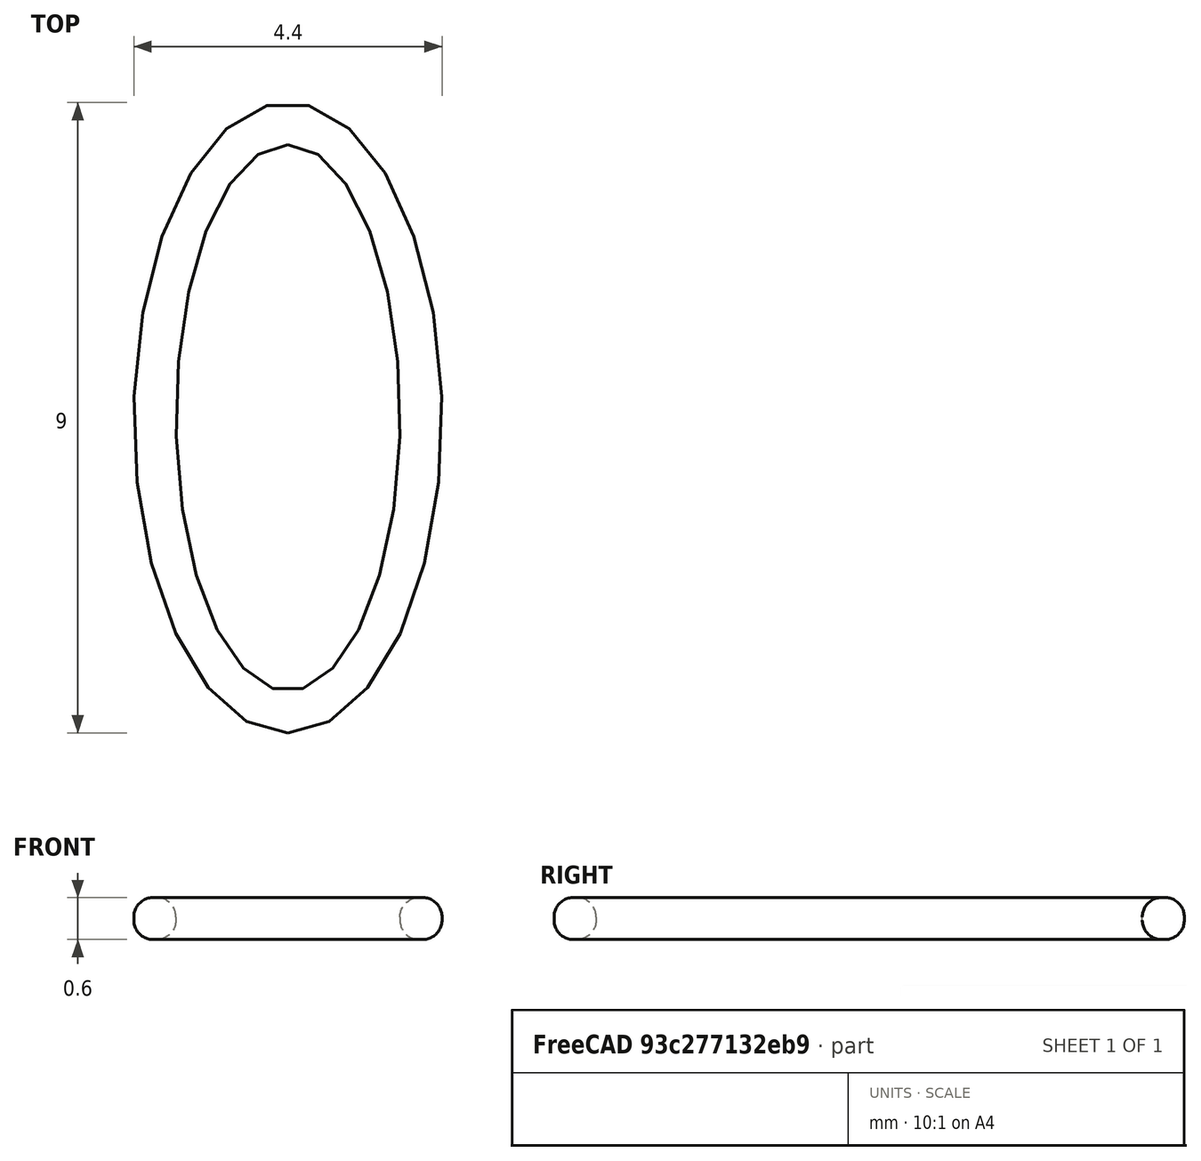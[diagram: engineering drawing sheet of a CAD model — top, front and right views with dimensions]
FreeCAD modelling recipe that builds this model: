
FCSTD DOCUMENT  (FreeCAD 0.16R6712 (Git))
Label: 0s
License: All rights reserved
LicenseURL: http://en.wikipedia.org/wiki/All_rights_reserved
objects: Sketcher::SketchObject×1, PartDesign::Pad×1, PartDesign::Fillet×1, Mesh::Feature×1
note: 4 computed .brp shape members not serialized (recipe doc carries the construction recipe); baked Part::Feature solids carry a one-line shape summary decoded from their .brp

FEATURE [Sketcher::SketchObject] Sketch
  sketch-geometry (10):
    g0: Ellipse CenterX=0 CenterY=4.5 CenterZ=0 NormalX=0 NormalY=0 NormalZ=1 MajorRadius=4.5 MinorRadius=2.2 AngleXU=-1.5708
    g1: LineSegment [constr] StartX=0 StartY=0 StartZ=0 EndX=0 EndY=9 EndZ=0
    g2: LineSegment [constr] StartX=2.2 StartY=4.5 StartZ=0 EndX=-2.2 EndY=4.5 EndZ=0
    g3: GeomPoint [constr] X=0 Y=0.574443 Z=0
    g4: GeomPoint [constr] X=0 Y=8.42556 Z=0
    g5: Ellipse CenterX=0 CenterY=4.5 CenterZ=0 NormalX=0 NormalY=0 NormalZ=1 MajorRadius=3.9 MinorRadius=1.6 AngleXU=1.5708
    g6: LineSegment [constr] StartX=0 StartY=8.4 StartZ=0 EndX=0 EndY=0.6 EndZ=0
    g7: LineSegment [constr] StartX=-1.6 StartY=4.5 StartZ=0 EndX=1.6 EndY=4.5 EndZ=0
    g8: GeomPoint [constr] X=0 Y=8.05668 Z=0
    g9: GeomPoint [constr] X=0 Y=0.943316 Z=0
  constraints (11):
    c: InternalAlignment(g1-g4 -> g0) x4
    c: PointOnObject(g0,g-2)
    c: PointOnObject(g-1,g0)
    c: Distance(g2,g0) = 2.2
    c: PointOnObject(g1,g-2)
    c: InternalAlignment(g6-g9 -> g5) x4
    c: Coincident(g5,g0)
    c: DistanceY(g-1,g0) = 4.5
    c: DistanceY(g6,g1) = 0.6
    c: DistanceX(g7,g2) = 0.6
    c: PointOnObject(g6,g-2)
FEATURE [PartDesign::Pad] Pad
  Length = 0.6
  Length2 = 100
  Midplane = true
  Sketch = -> Sketch
  Type = 0
FEATURE [PartDesign::Fillet] Fillet
  Base = -> Pad [Edge3,Edge6,Edge2,Edge5]
  Radius = 0.277
FEATURE [Mesh::Feature] Mesh  label="Fillet (Meshed)"
